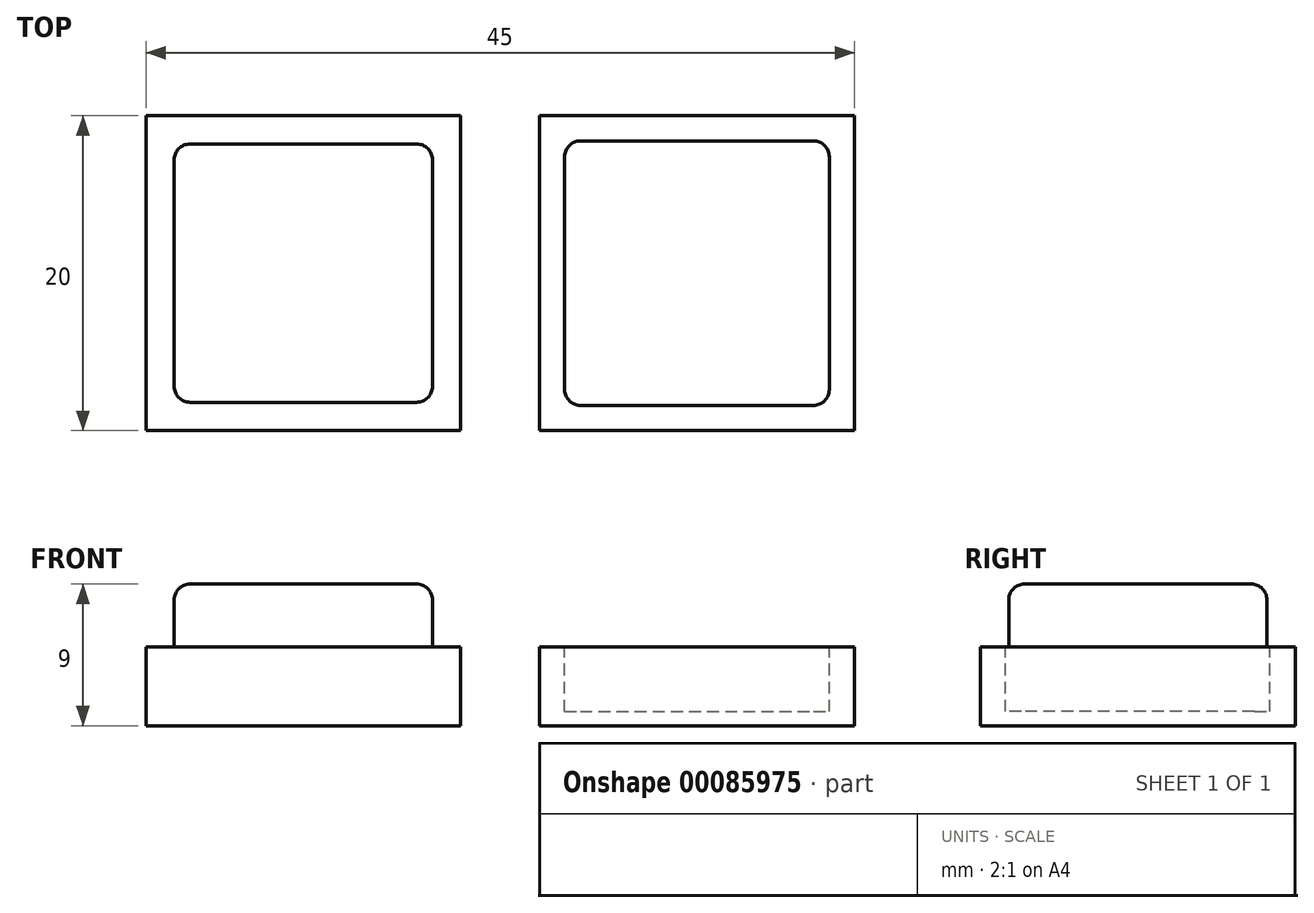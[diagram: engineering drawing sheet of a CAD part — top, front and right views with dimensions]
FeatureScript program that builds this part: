
annotation { "Feature Type Name" : "Feature", "Feature Type Description" : "" }
export const myFeature = defineFeature(function(context is Context, id is Id, definition is map)
    precondition{}
    {
        {
            var Q0;
            Q0=qCreatedBy(makeId("Top.planeOp"),FACE);
            var sketch = newSketch(context, id + "F0", { "sketchPlane" : qUnion([Q0])});
            skLineSegment(sketch, "E0.bottom", {"start": v(0, 0) * mm, "end": v(-20, 0) * mm});
            skLineSegment(sketch, "E0.top", {"start": v(0, 20) * mm, "end": v(-20, 20) * mm});
            skLineSegment(sketch, "E0.left", {"start": v(0, 0) * mm, "end": v(0, 20) * mm});
            skLineSegment(sketch, "E0.right", {"start": v(-20, 0) * mm, "end": v(-20, 20) * mm});
            skSolve(sketch);
        }
        {
            var Q0;
            Q0=makeQuery(id+"F0.imprint","IMPRINT",FACE,{"disambiguationData":[TD([[makeQuery(id+"F0.imprint","IMPRINT",EDGE,{"derivedFrom":sQuery(id+"F0.wireOp",EDGE,"E0.bottom")}),-1.0]])]});
            extrude(context, id + "F1", {"entities" : qUnion([Q0]), "depth" : 5 * mm});
        }
        {
            var Q0;
            Q0=makeQuery(id+"F1.opExtrude","CAP_FACE",FACE,{"disambiguationData":[OSD([sQuery(id+"F0.wireOp",EDGE,"E0.bottom"),sQuery(id+"F0.wireOp",EDGE,"E0.top"),sQuery(id+"F0.wireOp",EDGE,"E0.left"),sQuery(id+"F0.wireOp",EDGE,"E0.right")])],"isStart":false});
            var sketch = newSketch(context, id + "F2", { "sketchPlane" : qUnion([Q0])});
            skLineSegment(sketch, "E1.bottom", {"start": v(-1.8, 1.8) * mm, "end": v(-18.2, 1.8) * mm});
            skLineSegment(sketch, "E1.top", {"start": v(-1.8, 18.2) * mm, "end": v(-18.2, 18.2) * mm});
            skLineSegment(sketch, "E1.left", {"start": v(-1.8, 1.8) * mm, "end": v(-1.8, 18.2) * mm});
            skLineSegment(sketch, "E1.right", {"start": v(-18.2, 1.8) * mm, "end": v(-18.2, 18.2) * mm});
            skSolve(sketch);
        }
        {
            var Q0;
            Q0 = qSketchRegion(id + "F2", true);
            extrude(context, id + "F3", {"entities" : qUnion([Q0]), "operationType" : NewBodyOperationType.ADD, "depth" : 4 * mm});
        }
        {
            var Q0;
            Q0=makeQuery(id+"F3.opExtrude","CAP_FACE",FACE,{"disambiguationData":[OSD([sQuery(id+"F2.wireOp",EDGE,"E1.bottom"),sQuery(id+"F2.wireOp",EDGE,"E1.top"),sQuery(id+"F2.wireOp",EDGE,"E1.left"),sQuery(id+"F2.wireOp",EDGE,"E1.right")])],"isStart":false});
            fillet(context, id + "F4", {"entities" : qUnion([Q0]), "radius" : 1 * mm, "tangentPropagation" : true, "allowEdgeOverflow" : false});
        }
        {
            var Q0;
            Q0=qCreatedBy(makeId("Top.planeOp"),FACE);
            var sketch = newSketch(context, id + "F5", { "sketchPlane" : qUnion([Q0])});
            skLineSegment(sketch, "E2.bottom", {"start": v(5, 0) * mm, "end": v(25, 0) * mm});
            skLineSegment(sketch, "E2.top", {"start": v(5, 20) * mm, "end": v(25, 20) * mm});
            skLineSegment(sketch, "E2.left", {"start": v(5, 0) * mm, "end": v(5, 20) * mm});
            skLineSegment(sketch, "E2.right", {"start": v(25, 0) * mm, "end": v(25, 20) * mm});
            skSolve(sketch);
        }
        {
            var Q0;
            Q0 = qSketchRegion(id + "F5", true);
            extrude(context, id + "F6", {"entities" : qUnion([Q0]), "depth" : 5 * mm});
        }
        {
            var Q0;
            Q0=makeQuery(id+"F6.opExtrude","CAP_FACE",FACE,{"disambiguationData":[OSD([sQuery(id+"F5.wireOp",EDGE,"E2.bottom"),sQuery(id+"F5.wireOp",EDGE,"E2.top"),sQuery(id+"F5.wireOp",EDGE,"E2.left"),sQuery(id+"F5.wireOp",EDGE,"E2.right")])],"isStart":false});
            var sketch = newSketch(context, id + "F7", { "sketchPlane" : qUnion([Q0])});
            skLineSegment(sketch, "E3.bottom", {"start": v(6.6, 18.4) * mm, "end": v(23.4, 18.4) * mm});
            skLineSegment(sketch, "E3.top", {"start": v(6.6, 1.6) * mm, "end": v(23.4, 1.6) * mm});
            skLineSegment(sketch, "E3.left", {"start": v(6.6, 18.4) * mm, "end": v(6.6, 1.6) * mm});
            skLineSegment(sketch, "E3.right", {"start": v(23.4, 18.4) * mm, "end": v(23.4, 1.6) * mm});
            skSolve(sketch);
        }
        {
            var Q0;
            Q0 = qSketchRegion(id + "F7", true);
            extrude(context, id + "F8", {"entities" : qUnion([Q0]), "operationType" : NewBodyOperationType.REMOVE, "oppositeDirection" : true, "depth" : 4.1 * mm});
        }
        {
            var Q0;
            Q0=makeQuery(id+"F3.opExtrude","SWEPT_EDGE",EDGE,{"disambiguationData":[OSD([sQuery(id+"F2.wireOp",EDGE,"E1.top"),sQuery(id+"F2.wireOp",EDGE,"E1.left")])]});
            var Q1;
            Q1=makeQuery(id+"F3.opExtrude","SWEPT_EDGE",EDGE,{"disambiguationData":[OSD([sQuery(id+"F2.wireOp",EDGE,"E1.bottom"),sQuery(id+"F2.wireOp",EDGE,"E1.left")])]});
            var Q2;
            Q2=makeQuery(id+"F3.opExtrude","SWEPT_EDGE",EDGE,{"disambiguationData":[OSD([sQuery(id+"F2.wireOp",EDGE,"E1.bottom"),sQuery(id+"F2.wireOp",EDGE,"E1.right")])]});
            var Q3;
            Q3=makeQuery(id+"F3.opExtrude","SWEPT_EDGE",EDGE,{"disambiguationData":[OSD([sQuery(id+"F2.wireOp",EDGE,"E1.top"),sQuery(id+"F2.wireOp",EDGE,"E1.right")])]});
            fillet(context, id + "F9", {"entities" : qUnion([Q0, Q1, Q2, Q3]), "radius" : 1 * mm, "tangentPropagation" : true, "allowEdgeOverflow" : false});
        }
        {
            var Q0;
            Q0=makeQuery(id+"F8.boolean.opBoolean","COPY",EDGE,{"derivedFrom":makeQuery(id+"F8.opExtrude","SWEPT_EDGE",EDGE,{"disambiguationData":[OSD([sQuery(id+"F7.wireOp",EDGE,"E3.bottom"),sQuery(id+"F7.wireOp",EDGE,"E3.left")])]})});
            var Q1;
            Q1=makeQuery(id+"F8.boolean.opBoolean","COPY",EDGE,{"derivedFrom":makeQuery(id+"F8.opExtrude","SWEPT_EDGE",EDGE,{"disambiguationData":[OSD([sQuery(id+"F7.wireOp",EDGE,"E3.bottom"),sQuery(id+"F7.wireOp",EDGE,"E3.right")])]})});
            var Q2;
            Q2=makeQuery(id+"F8.boolean.opBoolean","COPY",EDGE,{"derivedFrom":makeQuery(id+"F8.opExtrude","SWEPT_EDGE",EDGE,{"disambiguationData":[OSD([sQuery(id+"F7.wireOp",EDGE,"E3.top"),sQuery(id+"F7.wireOp",EDGE,"E3.right")])]})});
            var Q3;
            Q3=makeQuery(id+"F8.boolean.opBoolean","COPY",EDGE,{"derivedFrom":makeQuery(id+"F8.opExtrude","SWEPT_EDGE",EDGE,{"disambiguationData":[OSD([sQuery(id+"F7.wireOp",EDGE,"E3.top"),sQuery(id+"F7.wireOp",EDGE,"E3.left")])]})});
            fillet(context, id + "F10", {"entities" : qUnion([Q0, Q1, Q2, Q3]), "radius" : 1 * mm, "tangentPropagation" : true, "allowEdgeOverflow" : false});
        }
    });
